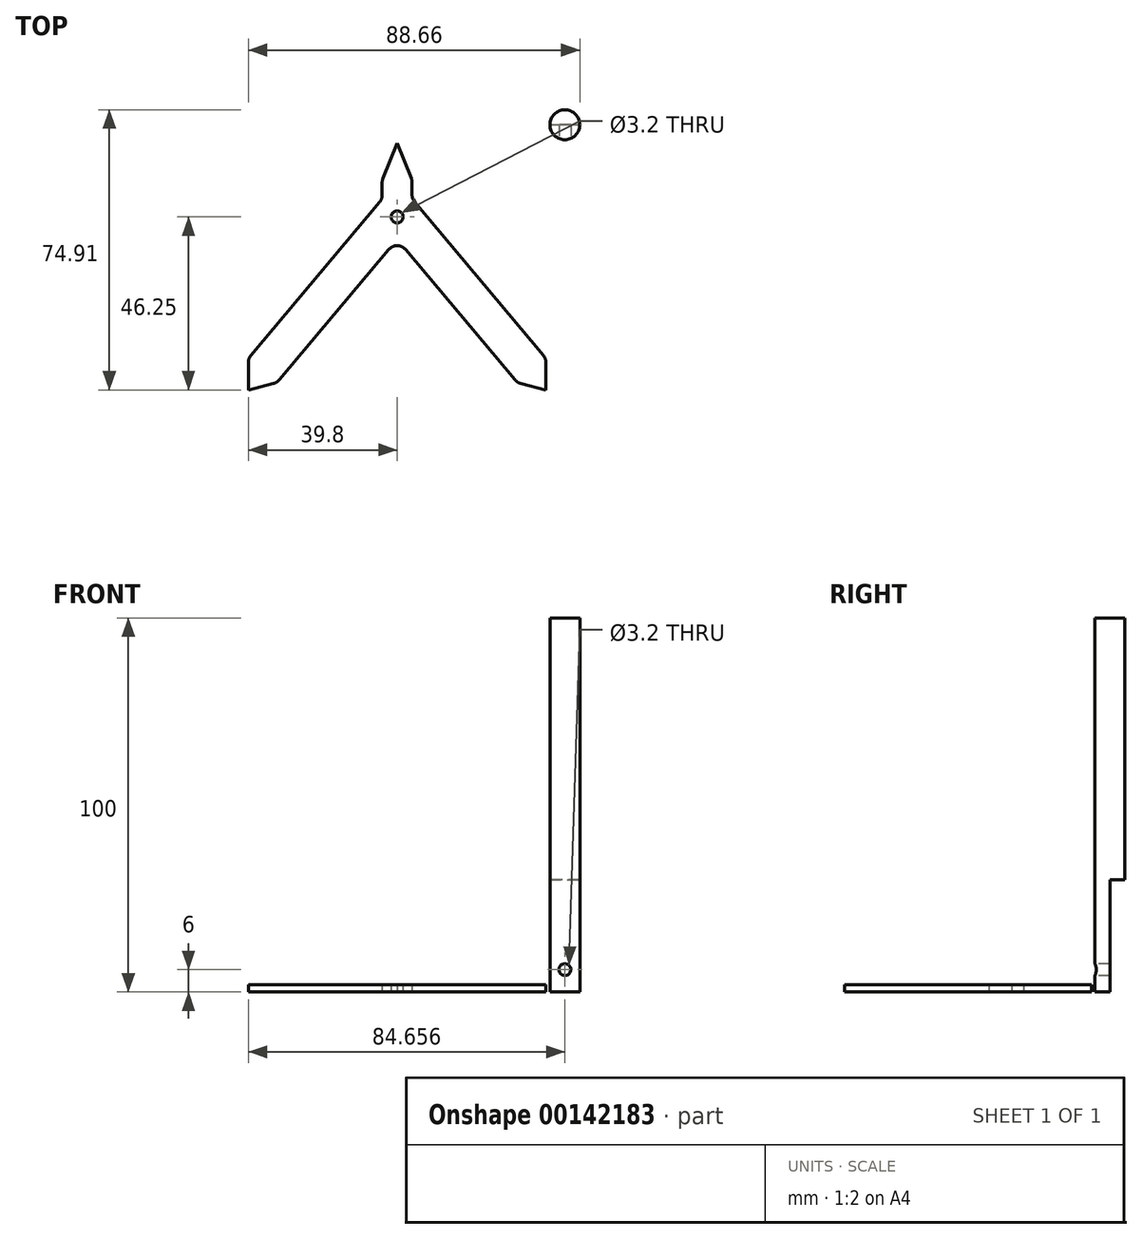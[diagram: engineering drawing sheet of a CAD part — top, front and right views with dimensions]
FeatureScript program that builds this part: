
annotation { "Feature Type Name" : "Feature", "Feature Type Description" : "" }
export const myFeature = defineFeature(function(context is Context, id is Id, definition is map)
    precondition{}
    {
        {
            var Q0;
            Q0=qCreatedBy(makeId("Top.planeOp"),FACE);
            var sketch = newSketch(context, id + "F0", { "sketchPlane" : qUnion([Q0])});
            skLineSegment(sketch, "E0", {"start": v(0, 39.7) * mm, "end": v(0, -51.9) * mm, "construction": true});
            skLineSegment(sketch, "E1", {"start": v(0, 0) * mm, "end": v(-32.14, -38.3) * mm});
            skLineSegment(sketch, "E2", {"start": v(-39.8, -31.87) * mm, "end": v(-4, 10.8) * mm});
            skLineSegment(sketch, "E3", {"start": v(-39.8, -31.87) * mm, "end": v(-39.8, -40.25) * mm});
            skLineSegment(sketch, "E4", {"start": v(-39.8, -40.25) * mm, "end": v(-32.14, -38.3) * mm});
            skLineSegment(sketch, "E5", {"start": v(-4, 10.8) * mm, "end": v(-4, 15.8) * mm});
            skLineSegment(sketch, "E6", {"start": v(-4, 15.8) * mm, "end": v(0, 25.8) * mm});
            skLineSegment(sketch, "E7.MirrorCS", {"start": v(39.8, -40.25) * mm, "end": v(32.14, -38.3) * mm});
            skLineSegment(sketch, "E8.MirrorCS", {"start": v(39.8, -31.87) * mm, "end": v(39.8, -40.25) * mm});
            skLineSegment(sketch, "E9.MirrorCS", {"start": v(4, 15.8) * mm, "end": v(0, 25.8) * mm});
            skLineSegment(sketch, "E10.MirrorCS", {"start": v(4, 10.8) * mm, "end": v(4, 15.8) * mm});
            skLineSegment(sketch, "E11.MirrorCS", {"start": v(0, 0) * mm, "end": v(32.14, -38.3) * mm});
            skLineSegment(sketch, "E12.MirrorCS", {"start": v(39.8, -31.87) * mm, "end": v(4, 10.8) * mm});
            skPoint(sketch, "E13", {"position": v(0, 6) * mm});
            skCircle(sketch, "E14", {"center": v(44.86, 30.66) * mm, "radius": 4 * mm});
            skLineSegment(sketch, "E15", {"start": v(40.86, 30.66) * mm, "end": v(48.86, 30.66) * mm});
            skCircle(sketch, "E16", {"center": v(0, 6) * mm, "radius": 1.6 * mm});
            skSolve(sketch);
        }
        {
            var Q0;
            Q0=makeQuery(id+"F0.imprint","IMPRINT",FACE,{"disambiguationData":[TD([[makeQuery(id+"F0.imprint","IMPRINT",EDGE,{"derivedFrom":sQuery(id+"F0.wireOp",EDGE,"E1")}),-1.0]])]});
            extrude(context, id + "F1", {"entities" : qUnion([Q0]), "depth" : 2 * mm});
        }
        {
            var Q0;
            Q0=makeQuery(id+"F0.imprint","IMPRINT",FACE,{"disambiguationData":[TD([[makeQuery(id+"F0.imprint","IMPRINT",EDGE,{"derivedFrom":sQuery(id+"F0.wireOp",EDGE,"E14")}),1.0]])]});
            extrude(context, id + "F2", {"entities" : qUnion([Q0]), "depth" : 100 * mm});
        }
        {
            var Q0;
            {var subQ0=sQuery(id+"F0.wireOp",EDGE,"E15");Q0=makeQuery(id+"F0.imprint","IMPRINT",FACE,{"disambiguationData":[TD([[makeQuery(id+"F0.imprint","IMPRINT",EDGE,{"derivedFrom":subQ0}),1.0]])]});}
            extrude(context, id + "F3", {"entities" : qUnion([Q0]), "operationType" : NewBodyOperationType.REMOVE, "depth" : 30 * mm});
        }
        {
            var Q0;
            Q0=makeQuery(id+"F3.boolean.opBoolean","COPY",FACE,{"derivedFrom":makeQuery(id+"F3.opExtrude","SWEPT_FACE",FACE,{"disambiguationData":[OSD([sQuery(id+"F0.wireOp",EDGE,"E15")])]})});
            var sketch = newSketch(context, id + "F4", { "sketchPlane" : qUnion([Q0])});
            skLineSegment(sketch, "E17", {"start": v(-44.86, 0) * mm, "end": v(-44.86, 23.3) * mm, "construction": true});
            skPoint(sketch, "E18", {"position": v(-44.86, 6) * mm});
            skSolve(sketch);
        }
        {
            var Q0;
            Q0=sQuery(id+"F4.wireOp",VERTEX,"E18");
            var Q1;
            Q1=makeQuery(id+"F2.opExtrude","SWEPT_BODY",BODY,{"disambiguationData":[OSD([sQuery(id+"F0.wireOp",EDGE,"E14")])]});
            hole(context, id + "F5", {"style" : HoleStyle.SIMPLE, "endStyle" : HoleEndStyle.THROUGH, "holeDiameter" : 3.2 * mm, "locations" : qUnion([Q0]), "scope" : qUnion([Q1]), "isTappedThrough" : true, "startStyle" : HoleStartStyle.PART});
        }
        {
            var Q0;
            Q0=makeQuery(id+"F1.opExtrude","SWEPT_EDGE",EDGE,{"disambiguationData":[OSD([sQuery(id+"F0.wireOp",EDGE,"E9.MirrorCS"),sQuery(id+"F0.wireOp",EDGE,"E10.MirrorCS")])]});
            var Q1;
            Q1=makeQuery(id+"F1.opExtrude","SWEPT_EDGE",EDGE,{"disambiguationData":[OSD([sQuery(id+"F0.wireOp",EDGE,"E10.MirrorCS"),sQuery(id+"F0.wireOp",EDGE,"E12.MirrorCS")])]});
            var Q2;
            Q2=makeQuery(id+"F1.opExtrude","SWEPT_EDGE",EDGE,{"disambiguationData":[OSD([sQuery(id+"F0.wireOp",EDGE,"E5"),sQuery(id+"F0.wireOp",EDGE,"E6")])]});
            var Q3;
            Q3=makeQuery(id+"F1.opExtrude","SWEPT_EDGE",EDGE,{"disambiguationData":[OSD([sQuery(id+"F0.wireOp",EDGE,"E2"),sQuery(id+"F0.wireOp",EDGE,"E5")])]});
            var Q4;
            Q4=makeQuery(id+"F1.opExtrude","SWEPT_EDGE",EDGE,{"disambiguationData":[OSD([sQuery(id+"F0.wireOp",EDGE,"E2"),sQuery(id+"F0.wireOp",EDGE,"E3")])]});
            var Q5;
            Q5=makeQuery(id+"F1.opExtrude","SWEPT_EDGE",EDGE,{"disambiguationData":[OSD([sQuery(id+"F0.wireOp",EDGE,"E1"),sQuery(id+"F0.wireOp",EDGE,"E4")])]});
            var Q6;
            Q6=makeQuery(id+"F1.opExtrude","SWEPT_EDGE",EDGE,{"disambiguationData":[OSD([sQuery(id+"F0.wireOp",EDGE,"E7.MirrorCS"),sQuery(id+"F0.wireOp",EDGE,"E11.MirrorCS")])]});
            var Q7;
            Q7=makeQuery(id+"F1.opExtrude","SWEPT_EDGE",EDGE,{"disambiguationData":[OSD([sQuery(id+"F0.wireOp",EDGE,"E8.MirrorCS"),sQuery(id+"F0.wireOp",EDGE,"E12.MirrorCS")])]});
            var Q8;
            Q8=makeQuery(id+"F1.opExtrude","SWEPT_EDGE",EDGE,{"disambiguationData":[OSD([sQuery(id+"F0.wireOp",EDGE,"E1"),sQuery(id+"F0.wireOp",EDGE,"E11.MirrorCS")])]});
            fillet(context, id + "F6", {"entities" : qUnion([Q0, Q1, Q2, Q3, Q4, Q5, Q6, Q7, Q8]), "radius" : 3 * mm, "tangentPropagation" : true, "allowEdgeOverflow" : false});
        }
    });
